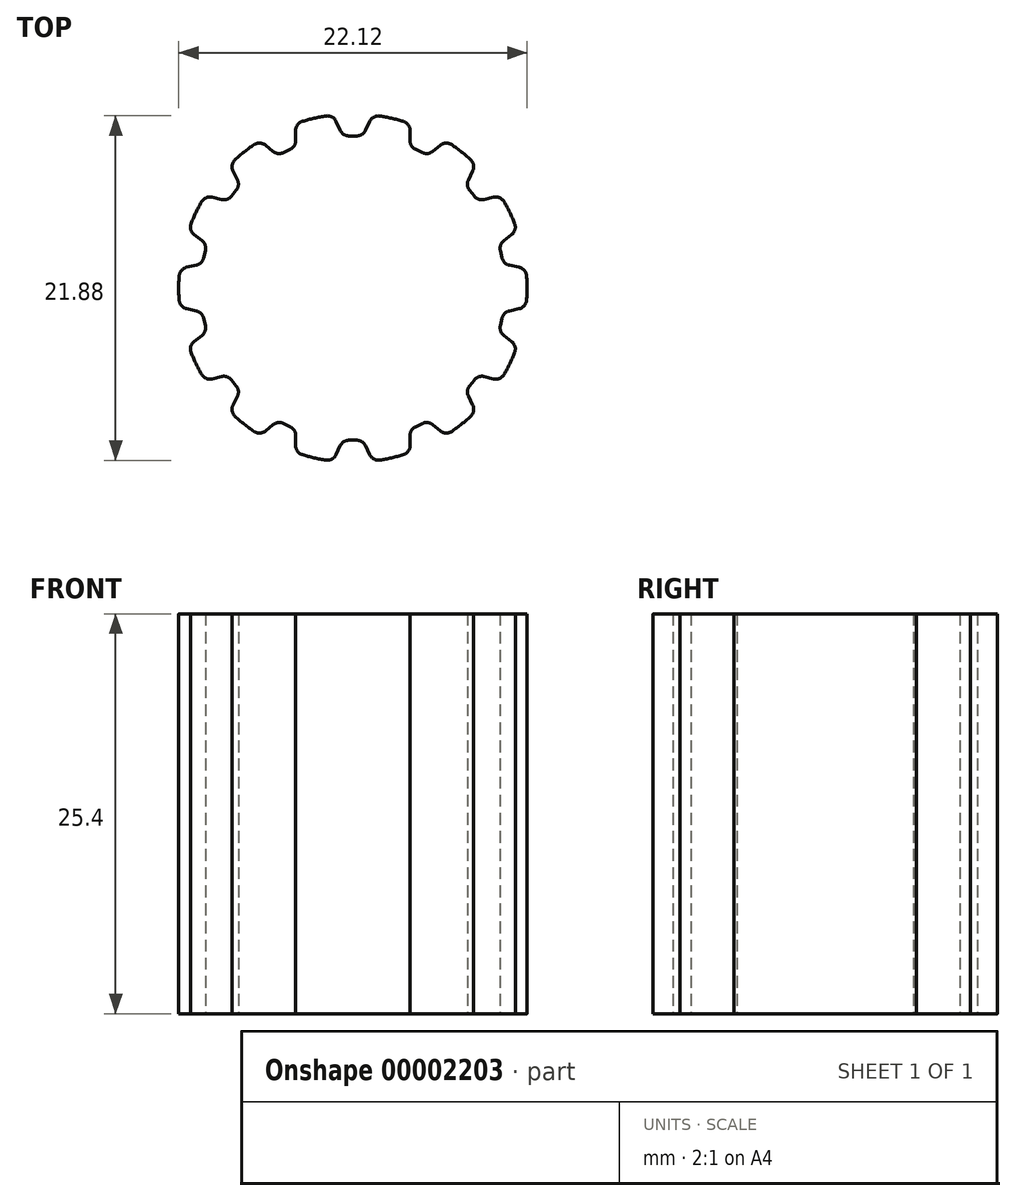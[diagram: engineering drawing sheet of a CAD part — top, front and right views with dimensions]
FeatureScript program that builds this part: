
annotation { "Feature Type Name" : "Feature", "Feature Type Description" : "" }
export const myFeature = defineFeature(function(context is Context, id is Id, definition is map)
    precondition{}
    {
        {
            var Q0;
            Q0=qCreatedBy(makeId("Top.planeOp"),FACE);
            var sketch = newSketch(context, id + "F0", { "sketchPlane" : qUnion([Q0])});
            skLineSegment(sketch, "E0.0", {"start": v(0.25, -9.66) * mm, "end": v(-0.25, -9.66) * mm});
            skArc(sketch, "E1.0", {"start": v(0.8, -10.02) * mm, "mid": v(0.57, -9.76) * mm, "end": v(0.25, -9.66) * mm});
            skLineSegment(sketch, "E2.0", {"start": v(1.06, -10.58) * mm, "end": v(0.8, -10.02) * mm});
            skArc(sketch, "E3.0", {"start": v(1.06, -10.58) * mm, "mid": v(1.33, -10.86) * mm, "end": v(1.71, -10.93) * mm});
            skArc(sketch, "E4.0", {"start": v(3.2, -10.59) * mm, "mid": v(2.46, -10.78) * mm, "end": v(1.71, -10.93) * mm});
            skArc(sketch, "E5.0", {"start": v(3.2, -10.59) * mm, "mid": v(3.52, -10.37) * mm, "end": v(3.63, -10) * mm});
            skLineSegment(sketch, "E6.0", {"start": v(3.63, -9.37) * mm, "end": v(3.63, -10) * mm});
            skArc(sketch, "E7.0", {"start": v(3.97, -8.81) * mm, "mid": v(3.72, -9.04) * mm, "end": v(3.63, -9.37) * mm});
            skLineSegment(sketch, "E8.0", {"start": v(4.42, -8.6) * mm, "end": v(3.97, -8.81) * mm});
            skArc(sketch, "E9.0", {"start": v(5.07, -8.68) * mm, "mid": v(4.75, -8.54) * mm, "end": v(4.42, -8.6) * mm});
            skLineSegment(sketch, "E10.0", {"start": v(5.55, -9.07) * mm, "end": v(5.07, -8.68) * mm});
            skArc(sketch, "E11.0", {"start": v(5.55, -9.07) * mm, "mid": v(5.91, -9.21) * mm, "end": v(6.28, -9.1) * mm});
            skArc(sketch, "E12.0", {"start": v(7.48, -8.15) * mm, "mid": v(6.9, -8.65) * mm, "end": v(6.28, -9.1) * mm});
            skArc(sketch, "E13.0", {"start": v(7.48, -8.15) * mm, "mid": v(7.67, -7.81) * mm, "end": v(7.61, -7.43) * mm});
            skLineSegment(sketch, "E14.0", {"start": v(7.33, -6.87) * mm, "end": v(7.61, -7.43) * mm});
            skArc(sketch, "E15.0", {"start": v(7.4, -6.22) * mm, "mid": v(7.27, -6.53) * mm, "end": v(7.33, -6.87) * mm});
            skLineSegment(sketch, "E16.0", {"start": v(7.7, -5.83) * mm, "end": v(7.4, -6.22) * mm});
            skArc(sketch, "E17.0", {"start": v(8.33, -5.62) * mm, "mid": v(7.99, -5.64) * mm, "end": v(7.7, -5.83) * mm});
            skLineSegment(sketch, "E18.0", {"start": v(8.94, -5.77) * mm, "end": v(8.33, -5.62) * mm});
            skArc(sketch, "E19.0", {"start": v(8.94, -5.77) * mm, "mid": v(9.32, -5.73) * mm, "end": v(9.61, -5.48) * mm});
            skArc(sketch, "E20.0", {"start": v(10.27, -4.1) * mm, "mid": v(9.97, -4.8) * mm, "end": v(9.61, -5.48) * mm});
            skArc(sketch, "E21.0", {"start": v(10.27, -4.1) * mm, "mid": v(10.3, -3.71) * mm, "end": v(10.08, -3.4) * mm});
            skLineSegment(sketch, "E22.0", {"start": v(9.59, -3) * mm, "end": v(10.08, -3.4) * mm});
            skArc(sketch, "E23.0", {"start": v(9.37, -2.4) * mm, "mid": v(9.39, -2.73) * mm, "end": v(9.59, -3) * mm});
            skLineSegment(sketch, "E24.0", {"start": v(9.48, -1.91) * mm, "end": v(9.37, -2.4) * mm});
            skArc(sketch, "E25.0", {"start": v(9.94, -1.45) * mm, "mid": v(9.64, -1.61) * mm, "end": v(9.48, -1.91) * mm});
            skPoint(sketch, "E26.0", {"position": v(9.94, -1.45) * mm});
            skLineSegment(sketch, "E27.0", {"start": v(10.56, -1.32) * mm, "end": v(9.94, -1.45) * mm});
            skArc(sketch, "E28.0", {"start": v(10.56, -1.32) * mm, "mid": v(10.89, -1.12) * mm, "end": v(11.04, -0.76) * mm});
            skArc(sketch, "E29.0", {"start": v(11.04, 0.76) * mm, "mid": v(11.06, 0) * mm, "end": v(11.04, -0.76) * mm});
            skArc(sketch, "E30.0", {"start": v(11.04, 0.76) * mm, "mid": v(10.89, 1.12) * mm, "end": v(10.56, 1.32) * mm});
            skLineSegment(sketch, "E31.0", {"start": v(9.94, 1.45) * mm, "end": v(10.56, 1.32) * mm});
            skArc(sketch, "E32.0", {"start": v(9.48, 1.91) * mm, "mid": v(9.64, 1.61) * mm, "end": v(9.94, 1.45) * mm});
            skLineSegment(sketch, "E33.0", {"start": v(9.37, 2.4) * mm, "end": v(9.48, 1.91) * mm});
            skArc(sketch, "E34.0", {"start": v(9.59, 3) * mm, "mid": v(9.39, 2.73) * mm, "end": v(9.37, 2.4) * mm});
            skLineSegment(sketch, "E35.0", {"start": v(10.08, 3.4) * mm, "end": v(9.59, 3) * mm});
            skArc(sketch, "E36.0", {"start": v(10.08, 3.4) * mm, "mid": v(10.3, 3.71) * mm, "end": v(10.27, 4.1) * mm});
            skArc(sketch, "E37.0", {"start": v(9.61, 5.48) * mm, "mid": v(9.97, 4.8) * mm, "end": v(10.27, 4.1) * mm});
            skArc(sketch, "E38.0", {"start": v(9.61, 5.48) * mm, "mid": v(9.32, 5.73) * mm, "end": v(8.94, 5.77) * mm});
            skLineSegment(sketch, "E39.0", {"start": v(8.33, 5.62) * mm, "end": v(8.94, 5.77) * mm});
            skArc(sketch, "E40.0", {"start": v(7.7, 5.83) * mm, "mid": v(7.99, 5.64) * mm, "end": v(8.33, 5.62) * mm});
            skPoint(sketch, "E41.0", {"position": v(7.7, 5.83) * mm});
            skLineSegment(sketch, "E42.0", {"start": v(7.4, 6.22) * mm, "end": v(7.7, 5.83) * mm});
            skArc(sketch, "E43.0", {"start": v(7.33, 6.87) * mm, "mid": v(7.27, 6.53) * mm, "end": v(7.4, 6.22) * mm});
            skLineSegment(sketch, "E44.0", {"start": v(7.61, 7.43) * mm, "end": v(7.33, 6.87) * mm});
            skArc(sketch, "E45.0", {"start": v(7.61, 7.43) * mm, "mid": v(7.67, 7.81) * mm, "end": v(7.48, 8.15) * mm});
            skArc(sketch, "E46.0", {"start": v(6.28, 9.1) * mm, "mid": v(6.9, 8.65) * mm, "end": v(7.48, 8.15) * mm});
            skArc(sketch, "E47.0", {"start": v(6.28, 9.1) * mm, "mid": v(5.91, 9.21) * mm, "end": v(5.55, 9.07) * mm});
            skLineSegment(sketch, "E48.0", {"start": v(5.07, 8.68) * mm, "end": v(5.55, 9.07) * mm});
            skArc(sketch, "E49.0", {"start": v(4.42, 8.6) * mm, "mid": v(4.75, 8.54) * mm, "end": v(5.07, 8.68) * mm});
            skLineSegment(sketch, "E50.0", {"start": v(3.97, 8.81) * mm, "end": v(4.42, 8.6) * mm});
            skArc(sketch, "E51.0", {"start": v(3.63, 9.37) * mm, "mid": v(3.72, 9.04) * mm, "end": v(3.97, 8.81) * mm});
            skLineSegment(sketch, "E52.0", {"start": v(3.63, 10) * mm, "end": v(3.63, 9.37) * mm});
            skArc(sketch, "E53.0", {"start": v(3.63, 10) * mm, "mid": v(3.52, 10.37) * mm, "end": v(3.2, 10.59) * mm});
            skArc(sketch, "E54.0", {"start": v(1.71, 10.93) * mm, "mid": v(2.46, 10.78) * mm, "end": v(3.2, 10.59) * mm});
            skArc(sketch, "E55.0", {"start": v(1.71, 10.93) * mm, "mid": v(1.33, 10.86) * mm, "end": v(1.06, 10.58) * mm});
            skLineSegment(sketch, "E56.0", {"start": v(0.8, 10.02) * mm, "end": v(1.06, 10.58) * mm});
            skArc(sketch, "E57.0", {"start": v(0.25, 9.66) * mm, "mid": v(0.57, 9.76) * mm, "end": v(0.8, 10.02) * mm});
            skLineSegment(sketch, "E58.0", {"start": v(-0.25, 9.66) * mm, "end": v(0.25, 9.66) * mm});
            skArc(sketch, "E59.0", {"start": v(-0.8, 10.02) * mm, "mid": v(-0.57, 9.76) * mm, "end": v(-0.25, 9.66) * mm});
            skLineSegment(sketch, "E60.0", {"start": v(-1.06, 10.58) * mm, "end": v(-0.8, 10.02) * mm});
            skArc(sketch, "E61.0", {"start": v(-1.06, 10.58) * mm, "mid": v(-1.33, 10.86) * mm, "end": v(-1.71, 10.93) * mm});
            skArc(sketch, "E62.0", {"start": v(-3.2, 10.59) * mm, "mid": v(-2.46, 10.78) * mm, "end": v(-1.71, 10.93) * mm});
            skLineSegment(sketch, "E63.0", {"start": v(-3.63, 9.37) * mm, "end": v(-3.63, 10) * mm});
            skArc(sketch, "E63.1", {"start": v(-3.97, 8.81) * mm, "mid": v(-3.72, 9.04) * mm, "end": v(-3.63, 9.37) * mm});
            skLineSegment(sketch, "E63.2", {"start": v(-4.42, 8.6) * mm, "end": v(-3.97, 8.81) * mm});
            skArc(sketch, "E63.3", {"start": v(-5.07, 8.68) * mm, "mid": v(-4.75, 8.54) * mm, "end": v(-4.42, 8.6) * mm});
            skLineSegment(sketch, "E63.4", {"start": v(-5.55, 9.07) * mm, "end": v(-5.07, 8.68) * mm});
            skArc(sketch, "E63.5", {"start": v(-5.55, 9.07) * mm, "mid": v(-5.91, 9.21) * mm, "end": v(-6.28, 9.1) * mm});
            skArc(sketch, "E63.6", {"start": v(-7.48, 8.15) * mm, "mid": v(-6.9, 8.65) * mm, "end": v(-6.28, 9.1) * mm});
            skArc(sketch, "E63.7", {"start": v(-7.48, 8.15) * mm, "mid": v(-7.67, 7.81) * mm, "end": v(-7.61, 7.43) * mm});
            skLineSegment(sketch, "E63.8", {"start": v(-7.33, 6.87) * mm, "end": v(-7.61, 7.43) * mm});
            skArc(sketch, "E63.9", {"start": v(-7.4, 6.22) * mm, "mid": v(-7.27, 6.53) * mm, "end": v(-7.33, 6.87) * mm});
            skLineSegment(sketch, "E63.10", {"start": v(-7.7, 5.83) * mm, "end": v(-7.4, 6.22) * mm});
            skArc(sketch, "E63.11", {"start": v(-8.33, 5.62) * mm, "mid": v(-7.99, 5.64) * mm, "end": v(-7.7, 5.83) * mm});
            skLineSegment(sketch, "E63.12", {"start": v(-8.94, 5.77) * mm, "end": v(-8.33, 5.62) * mm});
            skArc(sketch, "E63.13", {"start": v(-8.94, 5.77) * mm, "mid": v(-9.32, 5.73) * mm, "end": v(-9.61, 5.48) * mm});
            skArc(sketch, "E63.14", {"start": v(-10.27, 4.1) * mm, "mid": v(-9.97, 4.8) * mm, "end": v(-9.61, 5.48) * mm});
            skArc(sketch, "E63.15", {"start": v(-10.27, 4.1) * mm, "mid": v(-10.3, 3.71) * mm, "end": v(-10.08, 3.4) * mm});
            skLineSegment(sketch, "E63.16", {"start": v(-9.59, 3) * mm, "end": v(-10.08, 3.4) * mm});
            skArc(sketch, "E63.17", {"start": v(-9.37, 2.4) * mm, "mid": v(-9.39, 2.73) * mm, "end": v(-9.59, 3) * mm});
            skLineSegment(sketch, "E63.18", {"start": v(-9.48, 1.91) * mm, "end": v(-9.37, 2.4) * mm});
            skArc(sketch, "E63.19", {"start": v(-9.94, 1.45) * mm, "mid": v(-9.64, 1.61) * mm, "end": v(-9.48, 1.91) * mm});
            skArc(sketch, "E63.20", {"start": v(-10.56, 1.32) * mm, "mid": v(-10.89, 1.12) * mm, "end": v(-11.04, 0.76) * mm});
            skLineSegment(sketch, "E63.21", {"start": v(-10.56, 1.32) * mm, "end": v(-9.94, 1.45) * mm});
            skArc(sketch, "E63.22", {"start": v(-11.04, -0.76) * mm, "mid": v(-11.06, 0) * mm, "end": v(-11.04, 0.76) * mm});
            skArc(sketch, "E63.23", {"start": v(-11.04, -0.76) * mm, "mid": v(-10.89, -1.12) * mm, "end": v(-10.56, -1.32) * mm});
            skLineSegment(sketch, "E63.24", {"start": v(-9.94, -1.45) * mm, "end": v(-10.56, -1.32) * mm});
            skArc(sketch, "E63.25", {"start": v(-9.48, -1.91) * mm, "mid": v(-9.64, -1.61) * mm, "end": v(-9.94, -1.45) * mm});
            skLineSegment(sketch, "E63.26", {"start": v(-9.37, -2.4) * mm, "end": v(-9.48, -1.91) * mm});
            skArc(sketch, "E63.27", {"start": v(-9.59, -3) * mm, "mid": v(-9.39, -2.73) * mm, "end": v(-9.37, -2.4) * mm});
            skLineSegment(sketch, "E63.28", {"start": v(-10.08, -3.4) * mm, "end": v(-9.59, -3) * mm});
            skArc(sketch, "E63.29", {"start": v(-10.08, -3.4) * mm, "mid": v(-10.3, -3.71) * mm, "end": v(-10.27, -4.1) * mm});
            skArc(sketch, "E63.30", {"start": v(-9.61, -5.48) * mm, "mid": v(-9.97, -4.8) * mm, "end": v(-10.27, -4.1) * mm});
            skArc(sketch, "E63.31", {"start": v(-9.61, -5.48) * mm, "mid": v(-9.32, -5.73) * mm, "end": v(-8.94, -5.77) * mm});
            skLineSegment(sketch, "E63.32", {"start": v(-8.33, -5.62) * mm, "end": v(-8.94, -5.77) * mm});
            skArc(sketch, "E63.33", {"start": v(-7.7, -5.83) * mm, "mid": v(-7.99, -5.64) * mm, "end": v(-8.33, -5.62) * mm});
            skLineSegment(sketch, "E63.34", {"start": v(-7.4, -6.22) * mm, "end": v(-7.7, -5.83) * mm});
            skArc(sketch, "E63.35", {"start": v(-7.33, -6.87) * mm, "mid": v(-7.27, -6.53) * mm, "end": v(-7.4, -6.22) * mm});
            skLineSegment(sketch, "E63.36", {"start": v(-7.61, -7.43) * mm, "end": v(-7.33, -6.87) * mm});
            skArc(sketch, "E63.37", {"start": v(-7.61, -7.43) * mm, "mid": v(-7.67, -7.81) * mm, "end": v(-7.48, -8.15) * mm});
            skArc(sketch, "E63.38", {"start": v(-6.28, -9.1) * mm, "mid": v(-6.9, -8.65) * mm, "end": v(-7.48, -8.15) * mm});
            skArc(sketch, "E63.39", {"start": v(-6.28, -9.1) * mm, "mid": v(-5.91, -9.21) * mm, "end": v(-5.55, -9.07) * mm});
            skLineSegment(sketch, "E63.40", {"start": v(-5.07, -8.68) * mm, "end": v(-5.55, -9.07) * mm});
            skArc(sketch, "E63.41", {"start": v(-4.42, -8.6) * mm, "mid": v(-4.75, -8.54) * mm, "end": v(-5.07, -8.68) * mm});
            skLineSegment(sketch, "E63.42", {"start": v(-3.97, -8.81) * mm, "end": v(-4.42, -8.6) * mm});
            skArc(sketch, "E63.43", {"start": v(-3.63, -9.37) * mm, "mid": v(-3.72, -9.04) * mm, "end": v(-3.97, -8.81) * mm});
            skLineSegment(sketch, "E63.44", {"start": v(-3.63, -10) * mm, "end": v(-3.63, -9.37) * mm});
            skArc(sketch, "E63.45", {"start": v(-3.63, -10) * mm, "mid": v(-3.52, -10.37) * mm, "end": v(-3.2, -10.59) * mm});
            skArc(sketch, "E63.46", {"start": v(-1.71, -10.93) * mm, "mid": v(-2.46, -10.78) * mm, "end": v(-3.2, -10.59) * mm});
            skArc(sketch, "E63.47", {"start": v(-1.71, -10.93) * mm, "mid": v(-1.33, -10.86) * mm, "end": v(-1.06, -10.58) * mm});
            skArc(sketch, "E64.0", {"start": v(-0.25, -9.66) * mm, "mid": v(-0.57, -9.76) * mm, "end": v(-0.8, -10.02) * mm});
            skLineSegment(sketch, "E65.0", {"start": v(-0.8, -10.02) * mm, "end": v(-1.06, -10.58) * mm});
            skArc(sketch, "E66.0", {"start": v(-3.2, 10.59) * mm, "mid": v(-3.52, 10.37) * mm, "end": v(-3.63, 10) * mm});
            skSolve(sketch);
        }
        {
            var Q0;
            Q0=makeQuery(id+"F0.imprint","IMPRINT",FACE,{"disambiguationData":[TD([[makeQuery(id+"F0.imprint","IMPRINT",EDGE,{"derivedFrom":sQuery(id+"F0.wireOp",EDGE,"E0.0")}),-1.0]])]});
            extrude(context, id + "F1", {"entities" : qUnion([Q0]), "depth" : 25.4 * mm});
        }
    });
